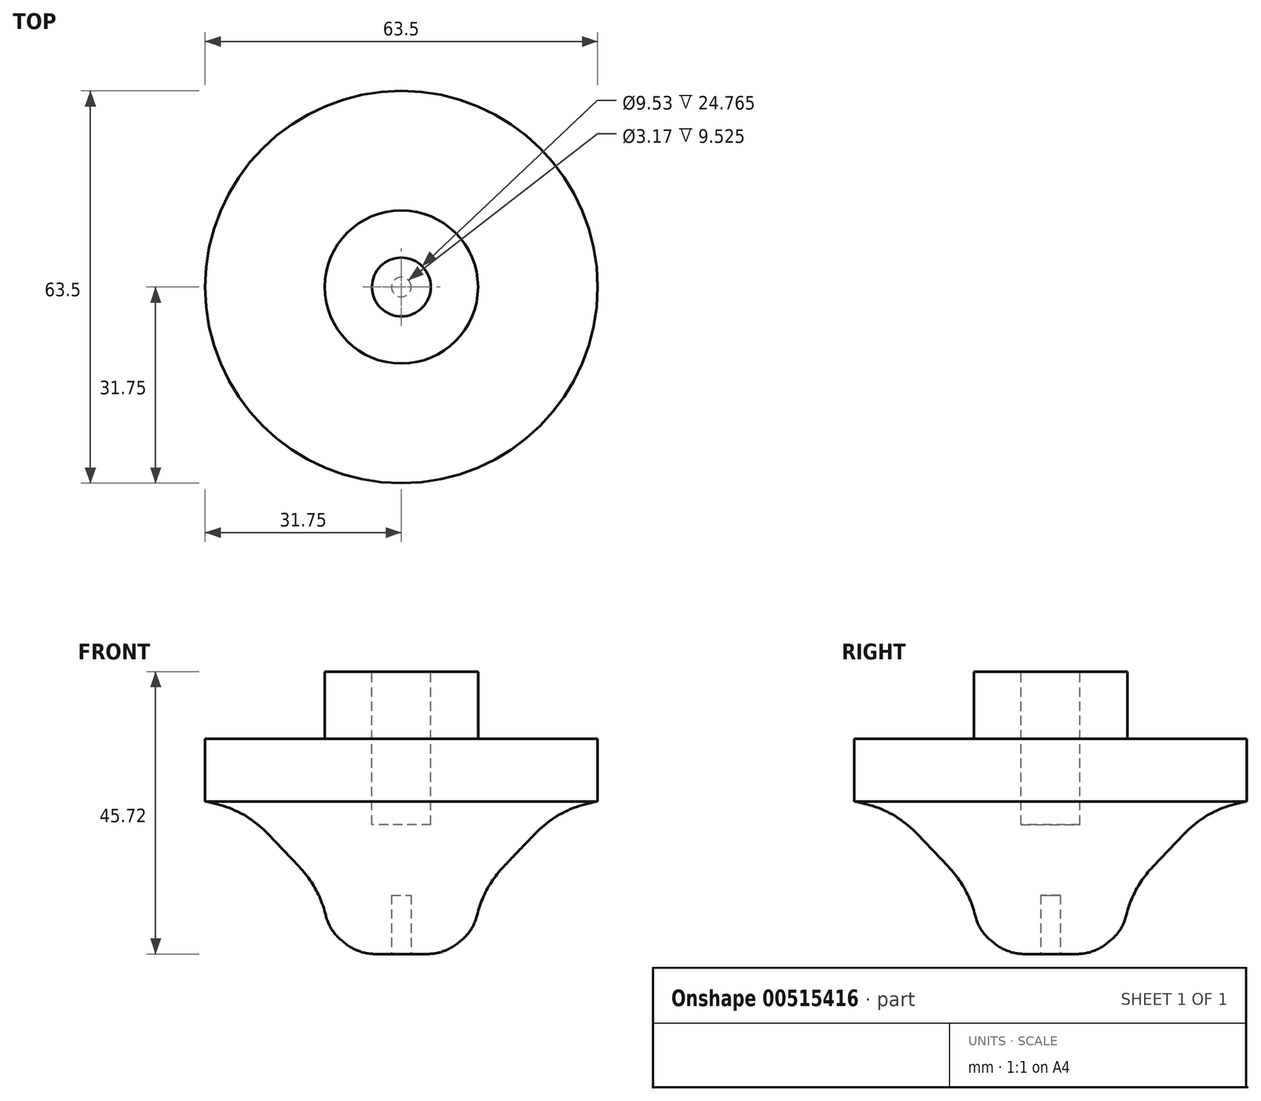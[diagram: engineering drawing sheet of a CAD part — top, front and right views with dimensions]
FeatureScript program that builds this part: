
annotation { "Feature Type Name" : "Feature", "Feature Type Description" : "" }
export const myFeature = defineFeature(function(context is Context, id is Id, definition is map)
    precondition{}
    {
        {
            var Q0;
            Q0=qCreatedBy(makeId("Front.planeOp"),FACE);
            var sketch = newSketch(context, id + "F0", { "sketchPlane" : qUnion([Q0])});
            skLineSegment(sketch, "E0", {"start": v(26.57, 24.66) * mm, "end": v(31.75, 24.66) * mm});
            skLineSegment(sketch, "E1", {"start": v(31.75, 24.66) * mm, "end": v(31.75, 34.82) * mm});
            skLineSegment(sketch, "E2", {"start": v(12.4, 45.72) * mm, "end": v(0, 45.72) * mm});
            skLineSegment(sketch, "E3", {"start": v(0, 45.72) * mm, "end": v(0, 0) * mm});
            skLineSegment(sketch, "E4", {"start": v(0, 0) * mm, "end": v(4.4, 0) * mm});
            skLineSegment(sketch, "E5", {"start": v(4.4, 0) * mm, "end": v(9.08, 6.3) * mm});
            skPoint(sketch, "E6.end.orphan", {"position": v(12.4, 34.82) * mm});
            skLineSegment(sketch, "E7", {"start": v(31.75, 34.82) * mm, "end": v(12.4, 34.82) * mm});
            skLineSegment(sketch, "E8", {"start": v(12.4, 34.82) * mm, "end": v(12.4, 45.72) * mm});
            skLineSegment(sketch, "E9", {"start": v(26.57, 24.66) * mm, "end": v(9.08, 6.3) * mm});
            skLineSegment(sketch, "E10", {"start": v(4.4, 0) * mm, "end": v(6.91, 0) * mm});
            skLineSegment(sketch, "E11", {"start": v(6.91, 0) * mm, "end": v(11.83, 3.9) * mm});
            skLineSegment(sketch, "E12", {"start": v(11.83, 3.9) * mm, "end": v(11.83, 9.2) * mm});
            skSolve(sketch);
        }
        {
            var Q0;
            Q0=qSketchRegion(id+"F0",true);
            var Q1;
            Q1=sQuery(id+"F0.wireOp",EDGE,"E3");
            revolve(context, id + "F1", {"entities" : qUnion([Q0]), "axis" : qUnion([Q1]), "revolveType" : RevolveType.FULL});
        }
        {
            var Q0;
            Q0=makeQuery(id+"F1.opRevolve","SWEPT_FACE",FACE,{"disambiguationData":[OSD([sQuery(id+"F0.wireOp",EDGE,"E2")])]});
            var sketch = newSketch(context, id + "F2", { "sketchPlane" : qUnion([Q0])});
            skCircle(sketch, "E13", {"center": v(0, 0) * mm, "radius": 4.76 * mm});
            skSolve(sketch);
        }
        {
            var Q0;
            Q0=qSketchRegion(id+"F2",true);
            extrude(context, id + "F3", {"entities" : qUnion([Q0]), "operationType" : NewBodyOperationType.REMOVE, "oppositeDirection" : true, "depth" : 24.76 * mm});
        }
        {
            var Q0;
            Q0=makeQuery(id+"F1.opRevolve","SWEPT_FACE",FACE,{"disambiguationData":[OSD([sQuery(id+"F0.wireOp",EDGE,"E4")])]});
            var sketch = newSketch(context, id + "F4", { "sketchPlane" : qUnion([Q0])});
            skCircle(sketch, "E14", {"center": v(0, 0) * mm, "radius": 1.59 * mm});
            skSolve(sketch);
        }
        {
            var Q0;
            Q0=qSketchRegion(id+"F4",true);
            extrude(context, id + "F5", {"entities" : qUnion([Q0]), "operationType" : NewBodyOperationType.REMOVE, "oppositeDirection" : true, "depth" : 9.52 * mm});
        }
        {
            var Q0;
            Q0=makeQuery(id+"F1.opRevolve","SWEPT_FACE",FACE,{"disambiguationData":[OSD([sQuery(id+"F0.wireOp",EDGE,"E9")])]});
            fillet(context, id + "F6", {"entities" : qUnion([Q0]), "radius" : 17.34 * mm, "tangentPropagation" : true, "allowEdgeOverflow" : false});
        }
        {
            var Q0;
            Q0=makeQuery(id+"F1.opRevolve","SWEPT_FACE",FACE,{"disambiguationData":[OSD([sQuery(id+"F0.wireOp",EDGE,"E11")])]});
            fillet(context, id + "F7", {"entities" : qUnion([Q0]), "radius" : 7.62 * mm, "tangentPropagation" : true, "allowEdgeOverflow" : false});
        }
    });
